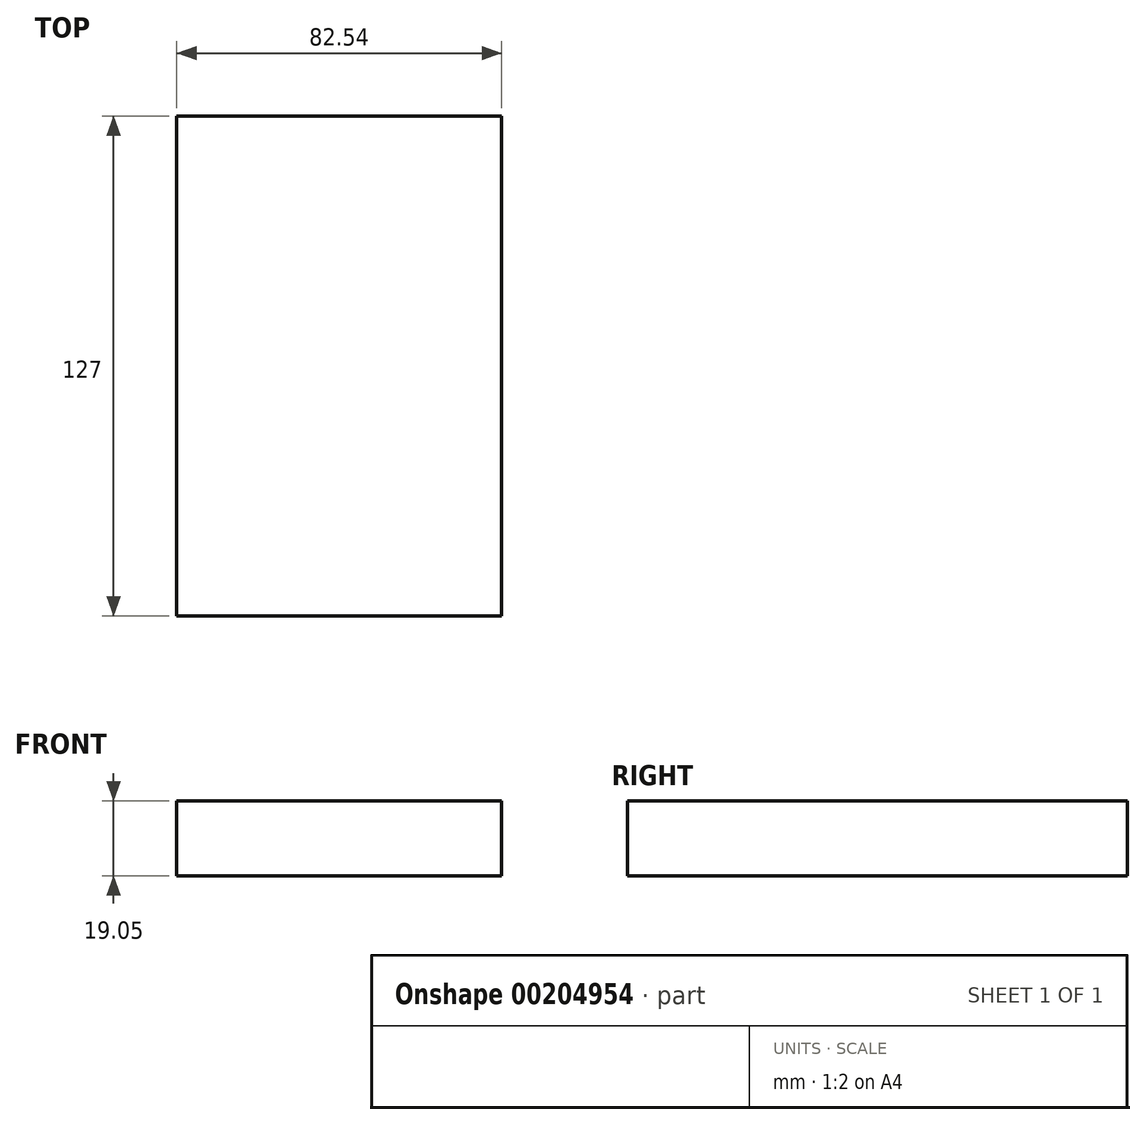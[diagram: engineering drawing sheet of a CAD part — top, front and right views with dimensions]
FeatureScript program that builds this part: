
annotation { "Feature Type Name" : "Feature", "Feature Type Description" : "" }
export const myFeature = defineFeature(function(context is Context, id is Id, definition is map)
    precondition{}
    {
        {
            var Q0;
            Q0=qCreatedBy(makeId("Top.planeOp"),FACE);
            var sketch = newSketch(context, id + "F0", { "sketchPlane" : qUnion([Q0])});
            skLineSegment(sketch, "E0.bottom", {"start": v(-41.27, 63.5) * mm, "end": v(41.28, 63.5) * mm});
            skLineSegment(sketch, "E0.top", {"start": v(-41.28, -63.5) * mm, "end": v(41.27, -63.5) * mm});
            skLineSegment(sketch, "E0.left", {"start": v(-41.27, 63.5) * mm, "end": v(-41.28, -63.5) * mm});
            skLineSegment(sketch, "E0.right", {"start": v(41.28, 63.5) * mm, "end": v(41.27, -63.5) * mm});
            skPoint(sketch, "E0.middle", {"position": v(0, 0) * mm});
            skSolve(sketch);
        }
        {
            var Q0;
            Q0=makeQuery(id+"F0.imprint","IMPRINT",FACE,{"disambiguationData":[TD([[makeQuery(id+"F0.imprint","IMPRINT",EDGE,{"derivedFrom":sQuery(id+"F0.wireOp",EDGE,"E0.bottom")}),-1.0]])]});
            extrude(context, id + "F1", {"entities" : qUnion([Q0]), "depth" : 19.05 * mm});
        }
    });
